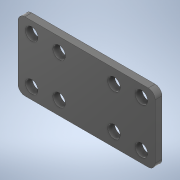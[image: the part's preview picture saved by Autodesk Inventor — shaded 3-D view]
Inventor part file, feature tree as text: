
AUTODESK INVENTOR PART (.ipt)
format: ipt  version: 2020 (Build 240168000, 168)  size: 148,992 bytes
history: native  units: mm
features: extrude x2, sketch x2, fillet x1
ambient origin geometry x8: Origin, YZ Plane, XZ Plane, XY Plane, X Axis, Y Axis, Z Axis, Center Point
bodies: Solid1 (feature_tree)
feature tree (5):
  extrude  "Extrusion1"  Depth=30.0mm
  extrude  "Extrusion2"  Depth=3.0mm
  fillet  "Fillet1"  Radius=5.5mm
  sketch  "Sketch1"  dims[d0=60.0mm d1=30.0mm]
  sketch  "Sketch2"  dims[d2=24.0mm d3=18.0mm d4=5.5mm d5=5.5mm d6=5.5mm d7=5.5mm d8=3.0mm d9=0.0mm d10=5.5mm d11=5.5mm d12=10.0mm d13=6.0mm d14=6.0mm d15=10.0mm d16=5.5mm d17=5.5mm d18=20.0mm d19=10.0mm d20=6.0mm d21=6.0mm d22=3.0mm d23=0.0mm d24=3.0mm]
